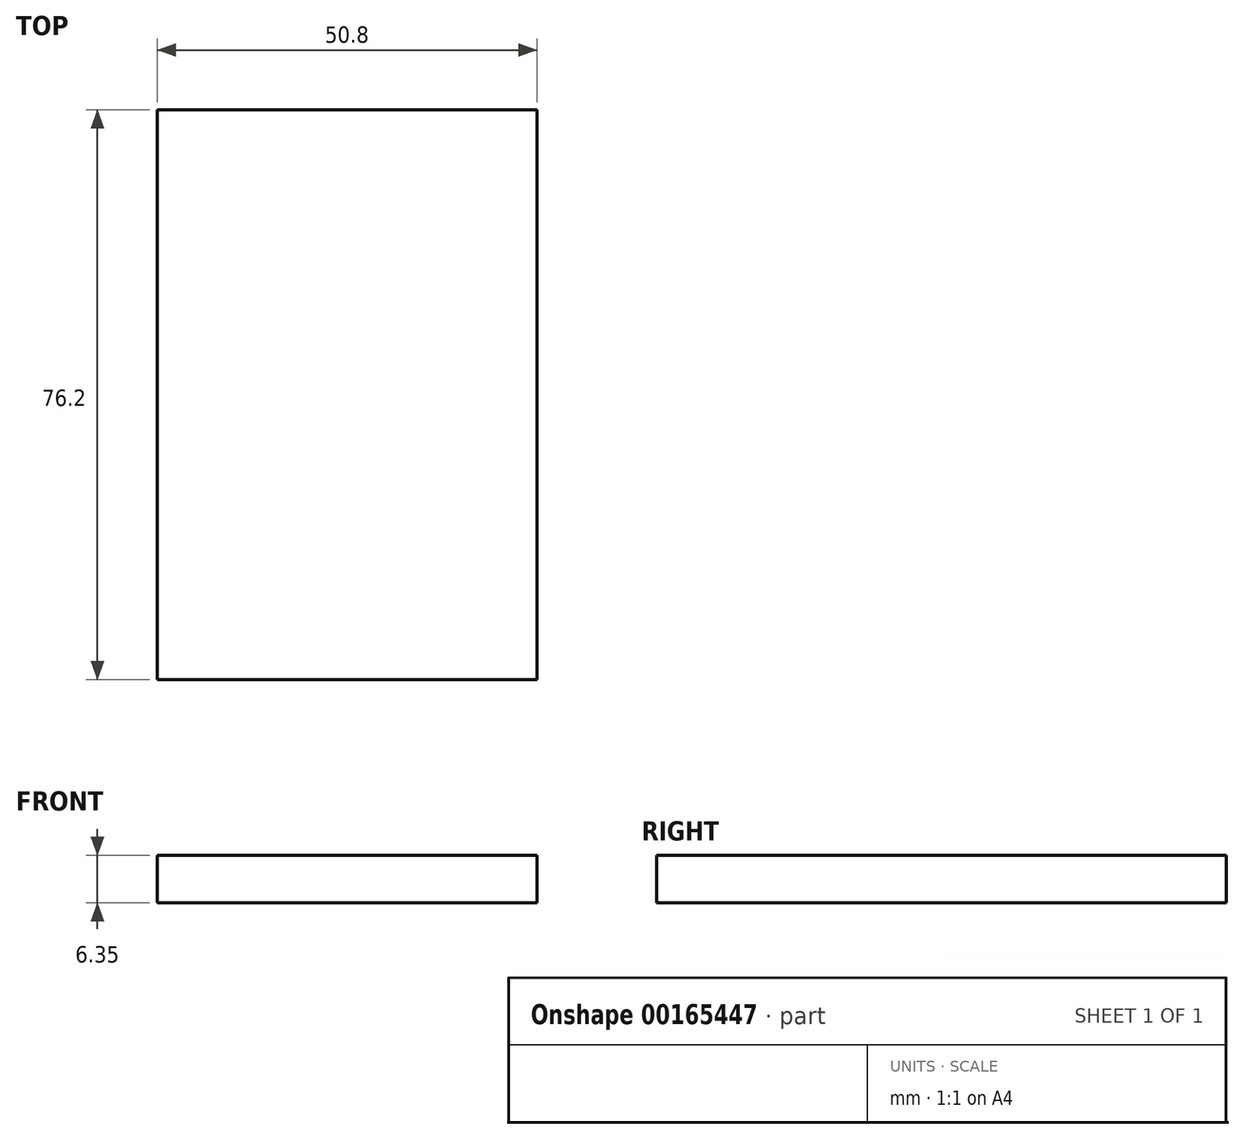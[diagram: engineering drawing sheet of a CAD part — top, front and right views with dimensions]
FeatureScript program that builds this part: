
annotation { "Feature Type Name" : "Feature", "Feature Type Description" : "" }
export const myFeature = defineFeature(function(context is Context, id is Id, definition is map)
    precondition{}
    {
        {
            var Q0;
            Q0=qCreatedBy(makeId("Top.planeOp"),FACE);
            var sketch = newSketch(context, id + "F0", { "sketchPlane" : qUnion([Q0])});
            skLineSegment(sketch, "E0.bottom", {"start": v(0, 0) * mm, "end": v(50.8, 0) * mm});
            skLineSegment(sketch, "E0.top", {"start": v(0, 76.2) * mm, "end": v(50.8, 76.2) * mm});
            skLineSegment(sketch, "E0.left", {"start": v(0, 0) * mm, "end": v(0, 76.2) * mm});
            skLineSegment(sketch, "E0.right", {"start": v(50.8, 0) * mm, "end": v(50.8, 76.2) * mm});
            skSolve(sketch);
        }
        {
            var Q0;
            Q0 = qSketchRegion(id + "F0", true);
            extrude(context, id + "F1", {"entities" : qUnion([Q0]), "depth" : 6.35 * mm});
        }
    });
